# Revit family: Site-Fencing-Tymetal_Corp-Structural_Cantilever_Slide_Gate-Ornamental
name_source: partatom
category: Site
revit_build: Autodesk Revit 2015 (Build: 20140606_1530(x64)
units: mm (PartAtom-declared; Revit-internal decimal feet)

## types (1)
- Standard
    Assembly Code = G2040100
    Bottom Guide Cover = No
    Catch Assembly Height Above Grade = 3' - 6"
    Clear Opening = 15' - 0"
    Cross Brace Length = 5' - 7 1/4"
    Description = Fortress Structural Cantilever Slide Gate with Ornamental Fencing
    Fence Offset from Grade = 0' - 5"
    Finish = Metal - Tymetal - Aluminum
    Finish Note = For additional powder coat color options, please contact Tymetal
    Frame Width = 0' - 2"
    Gate Documentation Link = http://www.tymetal.com
    Gate Height Clearances = 6' - 0"
    Hardware Finish = Metal - Tymetal - Aluminum
    Height = 6' - 0"
    Length = 22' - 6"
    Manufacturer = Tymetal Corp.
    Model = Ornamental
    Mount Clamp Extension from Gate = 0' - 2 3/8"
    Nominal Gate Height = 6' - 6"
    Notes = Single Clear Opening up to 40' and Double Clear Openings up to 80'
    Picket Count per Panel = 17
    Picket Height = 0' - 6"
    Picket Panel Count = 4
    Picket Panel Length = 5' - 7 1/4"
    Picket Spacing = 0' - 4"
    Picket Top = Yes
    Post Count = 2
    Post Diameter = 0' - 4"
    Post Height = 6' - 6"
    Post Radius = 0' - 2"
    Post Spacing = 6' - 7"
    Product Documentation Link = http://www.tymetal.com
    Product Page URL = http://www.tymetal.com
    Product data url = https://bimobject.com
    Single Gate Clearances = 15' - 0"
    Support Bracket = 3
    URL = http://www.tymetal.com

## geometry (parser evidence)
native form markers: Sweep x54
no freeform markers — native parametric forms only
